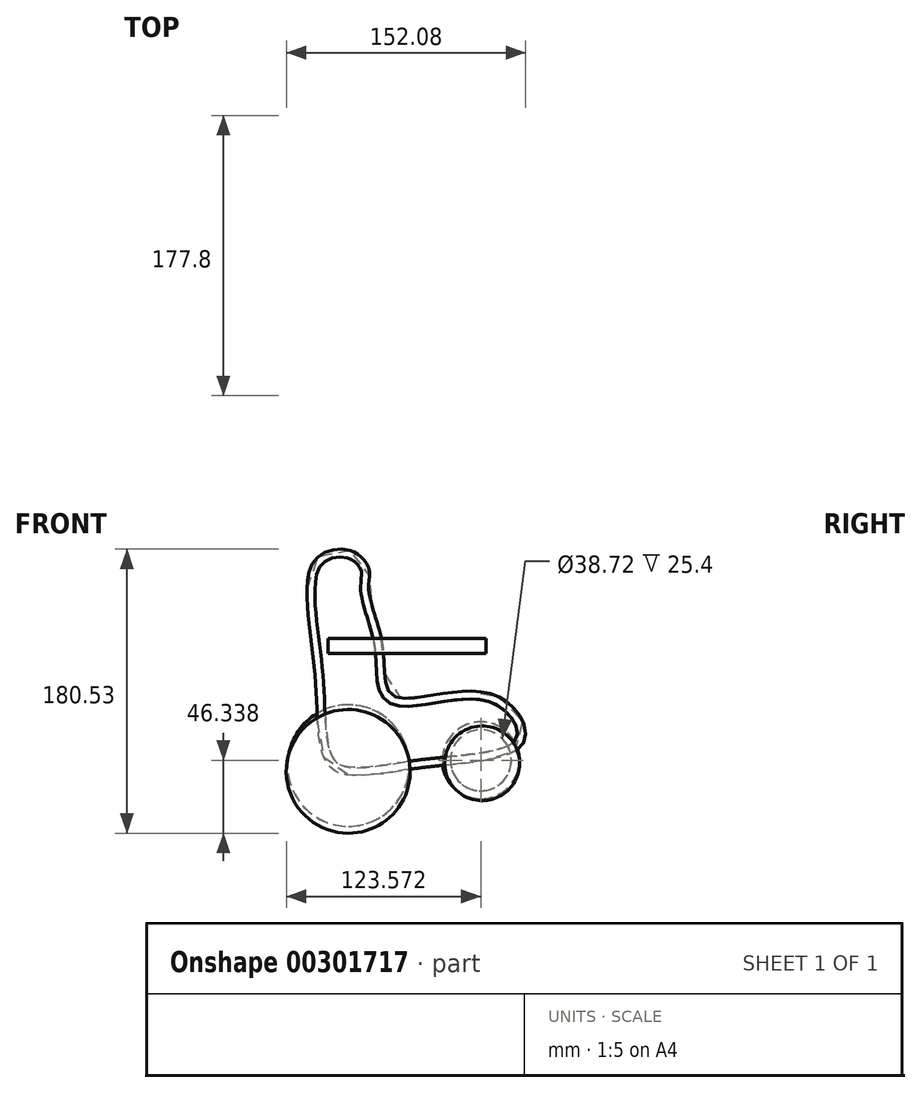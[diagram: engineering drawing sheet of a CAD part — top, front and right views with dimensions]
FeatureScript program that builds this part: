
annotation { "Feature Type Name" : "Feature", "Feature Type Description" : "" }
export const myFeature = defineFeature(function(context is Context, id is Id, definition is map)
    precondition{}
    {
        {
            var Q0;
            Q0=qCreatedBy(makeId("Front.planeOp"),FACE);
            var sketch = newSketch(context, id + "F0", { "sketchPlane" : qUnion([Q0])});
            skFitSpline(sketch, "E0", {"points": [v(-50.7, 69.52) * mm, v(-38.6, 57.69) * mm, v(-38.86, 44.5) * mm, v(-29.72, 7.13) * mm, v(-23, -23) * mm, v(38.32, -21.38) * mm, v(59.84, -52.04) * mm, v(-5.51, -68.45) * mm, v(-62.53, -68.98) * mm, v(-73.02, -9.28) * mm, v(-74.1, 62) * mm, v(-50.7, 69.52) * mm]});
            skSolve(sketch);
        }
        {
            var Q0;
            Q0=makeQuery(id+"F0.imprint","IMPRINT",FACE,{"disambiguationData":[TD([[makeQuery(id+"F0.imprint","IMPRINT",EDGE,{"derivedFrom":sQuery(id+"F0.wireOp",EDGE,"E0")}),-1.0]])]});
            extrude(context, id + "F1", {"entities" : qUnion([Q0]), "depth" : 127 * mm});
        }
        {
            var Q0;
            Q0=makeQuery(id+"F1.opExtrude","CAP_EDGE",EDGE,{"disambiguationData":[OSD([sQuery(id+"F0.wireOp",EDGE,"E0")])],"isStart":false});
            var Q1;
            Q1=makeQuery(id+"F1.opExtrude","CAP_EDGE",EDGE,{"disambiguationData":[OSD([sQuery(id+"F0.wireOp",EDGE,"E0")])],"isStart":true});
            fillet(context, id + "F2", {"entities" : qUnion([Q0, Q1]), "radius" : 5.08 * mm, "tangentPropagation" : true, "allowEdgeOverflow" : false});
        }
        {
            var Q0;
            Q0=qCreatedBy(makeId("Front.planeOp"),FACE);
            var sketch = newSketch(context, id + "F3", { "sketchPlane" : qUnion([Q0])});
            skCircle(sketch, "E1", {"center": v(32.4, -63.72) * mm, "radius": 24.44 * mm});
            skCircle(sketch, "E2", {"center": v(-51.77, -67.06) * mm, "radius": 38.6 * mm});
            skSolve(sketch);
        }
        {
            var Q0;
            Q0=makeQuery(id+"F3.imprint","IMPRINT",FACE,{"disambiguationData":[TD([[makeQuery(id+"F3.imprint","IMPRINT",EDGE,{"derivedFrom":sQuery(id+"F3.wireOp",EDGE,"E1")}),1.0]])]});
            var Q1;
            Q1=makeQuery(id+"F3.imprint","IMPRINT",FACE,{"disambiguationData":[TD([[makeQuery(id+"F3.imprint","IMPRINT",EDGE,{"derivedFrom":sQuery(id+"F3.wireOp",EDGE,"E2")}),1.0]])]});
            extrude(context, id + "F4", {"entities" : qUnion([Q0, Q1]), "operationType" : NewBodyOperationType.ADD, "oppositeDirection" : true, "depth" : 25.4 * mm});
        }
        {
            var Q0;
            Q0=makeQuery(id+"F4.opExtrude","CAP_EDGE",EDGE,{"disambiguationData":[OSD([sQuery(id+"F3.wireOp",EDGE,"E1")])],"isStart":false});
            var Q1;
            Q1=makeQuery(id+"F4.opExtrude","CAP_EDGE",EDGE,{"disambiguationData":[OSD([sQuery(id+"F3.wireOp",EDGE,"E2")])],"isStart":false});
            fillet(context, id + "F5", {"entities" : qUnion([Q0, Q1]), "radius" : 5.08 * mm, "tangentPropagation" : true, "allowEdgeOverflow" : false});
        }
        {
            var Q0;
            Q0=makeQuery(id+"F1.opExtrude","CAP_FACE",FACE,{"disambiguationData":[OSD([sQuery(id+"F0.wireOp",EDGE,"E0")])],"isStart":false});
            var sketch = newSketch(context, id + "F6", { "sketchPlane" : qUnion([Q0])});
            skCircle(sketch, "E3", {"center": v(33.19, -65.6) * mm, "radius": 23.74 * mm});
            skCircle(sketch, "E4", {"center": v(-51.86, -70.74) * mm, "radius": 39.31 * mm});
            skSolve(sketch);
        }
        {
            var Q0;
            {var subQ0=sQuery(id+"F6.wireOp",EDGE,"E4");var subQ1=sQuery(id+"F0.wireOp",EDGE,"E0");var subQ2=makeQuery(id+"F2.opFillet","BLEND_EDGE",EDGE,{"blendedFrom":[makeQuery(id+"F1.opExtrude","CAP_EDGE",EDGE,{"disambiguationData":[OSD([subQ1])],"isStart":false}),makeQuery(id+"F1.opExtrude","CAP_FACE",FACE,{"disambiguationData":[OSD([subQ1])],"isStart":false})],"blendedInto":[makeQuery(id+"F1.opExtrude","CAP_FACE",FACE,{"disambiguationData":[OSD([subQ1])],"isStart":false})]});var subQ3=makeQuery(id+"F6.imprint","INTERSECT",VERTEX,{"disambiguationData":[OD(0.0)],"derivedFrom":[subQ2,subQ0]});Q0=makeQuery(id+"F6.imprint","IMPRINT",FACE,{"disambiguationData":[TD([[makeQuery(id+"F6.imprint","IMPRINT",EDGE,{"disambiguationData":[TD([[subQ3,-1.0]])],"derivedFrom":subQ0}),1.0]])]});}
            var Q1;
            {var subQ0=sQuery(id+"F6.wireOp",EDGE,"E4");var subQ1=sQuery(id+"F0.wireOp",EDGE,"E0");var subQ2=makeQuery(id+"F2.opFillet","BLEND_EDGE",EDGE,{"blendedFrom":[makeQuery(id+"F1.opExtrude","CAP_EDGE",EDGE,{"disambiguationData":[OSD([subQ1])],"isStart":false}),makeQuery(id+"F1.opExtrude","CAP_FACE",FACE,{"disambiguationData":[OSD([subQ1])],"isStart":false})],"blendedInto":[makeQuery(id+"F1.opExtrude","CAP_FACE",FACE,{"disambiguationData":[OSD([subQ1])],"isStart":false})]});var subQ3=makeQuery(id+"F6.imprint","INTERSECT",VERTEX,{"disambiguationData":[OD(0.0)],"derivedFrom":[subQ2,subQ0]});Q1=makeQuery(id+"F6.imprint","IMPRINT",FACE,{"disambiguationData":[TD([[makeQuery(id+"F6.imprint","IMPRINT",EDGE,{"disambiguationData":[TD([[subQ3,1.0]])],"derivedFrom":subQ0}),1.0]])]});}
            var Q2;
            {var subQ0=sQuery(id+"F6.wireOp",EDGE,"E3");var subQ1=sQuery(id+"F0.wireOp",EDGE,"E0");var subQ2=makeQuery(id+"F2.opFillet","BLEND_EDGE",EDGE,{"blendedFrom":[makeQuery(id+"F1.opExtrude","CAP_EDGE",EDGE,{"disambiguationData":[OSD([subQ1])],"isStart":false}),makeQuery(id+"F1.opExtrude","CAP_FACE",FACE,{"disambiguationData":[OSD([subQ1])],"isStart":false})],"blendedInto":[makeQuery(id+"F1.opExtrude","CAP_FACE",FACE,{"disambiguationData":[OSD([subQ1])],"isStart":false})]});var subQ3=makeQuery(id+"F6.imprint","INTERSECT",VERTEX,{"disambiguationData":[OD(0.0)],"derivedFrom":[subQ2,subQ0]});Q2=makeQuery(id+"F6.imprint","IMPRINT",FACE,{"disambiguationData":[TD([[makeQuery(id+"F6.imprint","IMPRINT",EDGE,{"disambiguationData":[TD([[subQ3,-1.0]])],"derivedFrom":subQ0}),1.0]])]});}
            var Q3;
            {var subQ0=sQuery(id+"F6.wireOp",EDGE,"E3");var subQ1=sQuery(id+"F0.wireOp",EDGE,"E0");var subQ2=makeQuery(id+"F2.opFillet","BLEND_EDGE",EDGE,{"blendedFrom":[makeQuery(id+"F1.opExtrude","CAP_EDGE",EDGE,{"disambiguationData":[OSD([subQ1])],"isStart":false}),makeQuery(id+"F1.opExtrude","CAP_FACE",FACE,{"disambiguationData":[OSD([subQ1])],"isStart":false})],"blendedInto":[makeQuery(id+"F1.opExtrude","CAP_FACE",FACE,{"disambiguationData":[OSD([subQ1])],"isStart":false})]});var subQ3=makeQuery(id+"F6.imprint","INTERSECT",VERTEX,{"disambiguationData":[OD(0.0)],"derivedFrom":[subQ2,subQ0]});Q3=makeQuery(id+"F6.imprint","IMPRINT",FACE,{"disambiguationData":[TD([[makeQuery(id+"F6.imprint","IMPRINT",EDGE,{"disambiguationData":[TD([[subQ3,1.0]])],"derivedFrom":subQ0}),1.0]])]});}
            extrude(context, id + "F7", {"entities" : qUnion([Q0, Q1, Q2, Q3]), "operationType" : NewBodyOperationType.ADD, "depth" : 25.4 * mm});
        }
        {
            var Q0;
            Q0=makeQuery(id+"F7.opExtrude","CAP_EDGE",EDGE,{"disambiguationData":[OSD([sQuery(id+"F6.wireOp",EDGE,"E3")])],"isStart":false});
            var Q1;
            Q1=makeQuery(id+"F7.opExtrude","CAP_EDGE",EDGE,{"disambiguationData":[OSD([sQuery(id+"F6.wireOp",EDGE,"E4")])],"isStart":false});
            fillet(context, id + "F8", {"entities" : qUnion([Q0, Q1]), "radius" : 5.08 * mm, "tangentPropagation" : true, "allowEdgeOverflow" : false});
        }
        {
            var Q0;
            Q0=makeQuery(id+"F1.opExtrude","CAP_FACE",FACE,{"disambiguationData":[OSD([sQuery(id+"F0.wireOp",EDGE,"E0")])],"isStart":false});
            var sketch = newSketch(context, id + "F9", { "sketchPlane" : qUnion([Q0])});
            skLineSegment(sketch, "E5.bottom", {"start": v(-64.55, 4.18) * mm, "end": v(35.52, 4.18) * mm});
            skLineSegment(sketch, "E5.top", {"start": v(-64.55, 13.6) * mm, "end": v(35.52, 13.6) * mm});
            skLineSegment(sketch, "E5.left", {"start": v(-64.55, 4.18) * mm, "end": v(-64.55, 13.6) * mm});
            skLineSegment(sketch, "E5.right", {"start": v(35.52, 4.18) * mm, "end": v(35.52, 13.6) * mm});
            skSolve(sketch);
        }
        {
            var Q0;
            {var subQ0=sQuery(id+"F9.wireOp",EDGE,"E5.right");Q0=makeQuery(id+"F9.imprint","IMPRINT",FACE,{"disambiguationData":[TD([[makeQuery(id+"F9.imprint","IMPRINT",EDGE,{"derivedFrom":subQ0}),1.0]])]});}
            var Q1;
            {var subQ0=sQuery(id+"F9.wireOp",EDGE,"E5.left");Q1=makeQuery(id+"F9.imprint","IMPRINT",FACE,{"disambiguationData":[TD([[makeQuery(id+"F9.imprint","IMPRINT",EDGE,{"derivedFrom":subQ0}),-1.0]])]});}
            extrude(context, id + "F10", {"entities" : qUnion([Q0, Q1]), "operationType" : NewBodyOperationType.ADD, "depth" : 12.7 * mm});
        }
        {
            var Q0;
            Q0=makeQuery(id+"F4.opExtrude","CAP_FACE",FACE,{"disambiguationData":[OSD([sQuery(id+"F3.wireOp",EDGE,"E1")])],"isStart":false});
            extrude(context, id + "F11", {"entities" : qUnion([Q0]), "operationType" : NewBodyOperationType.REMOVE, "oppositeDirection" : true, "depth" : 25.4 * mm});
        }
    });
